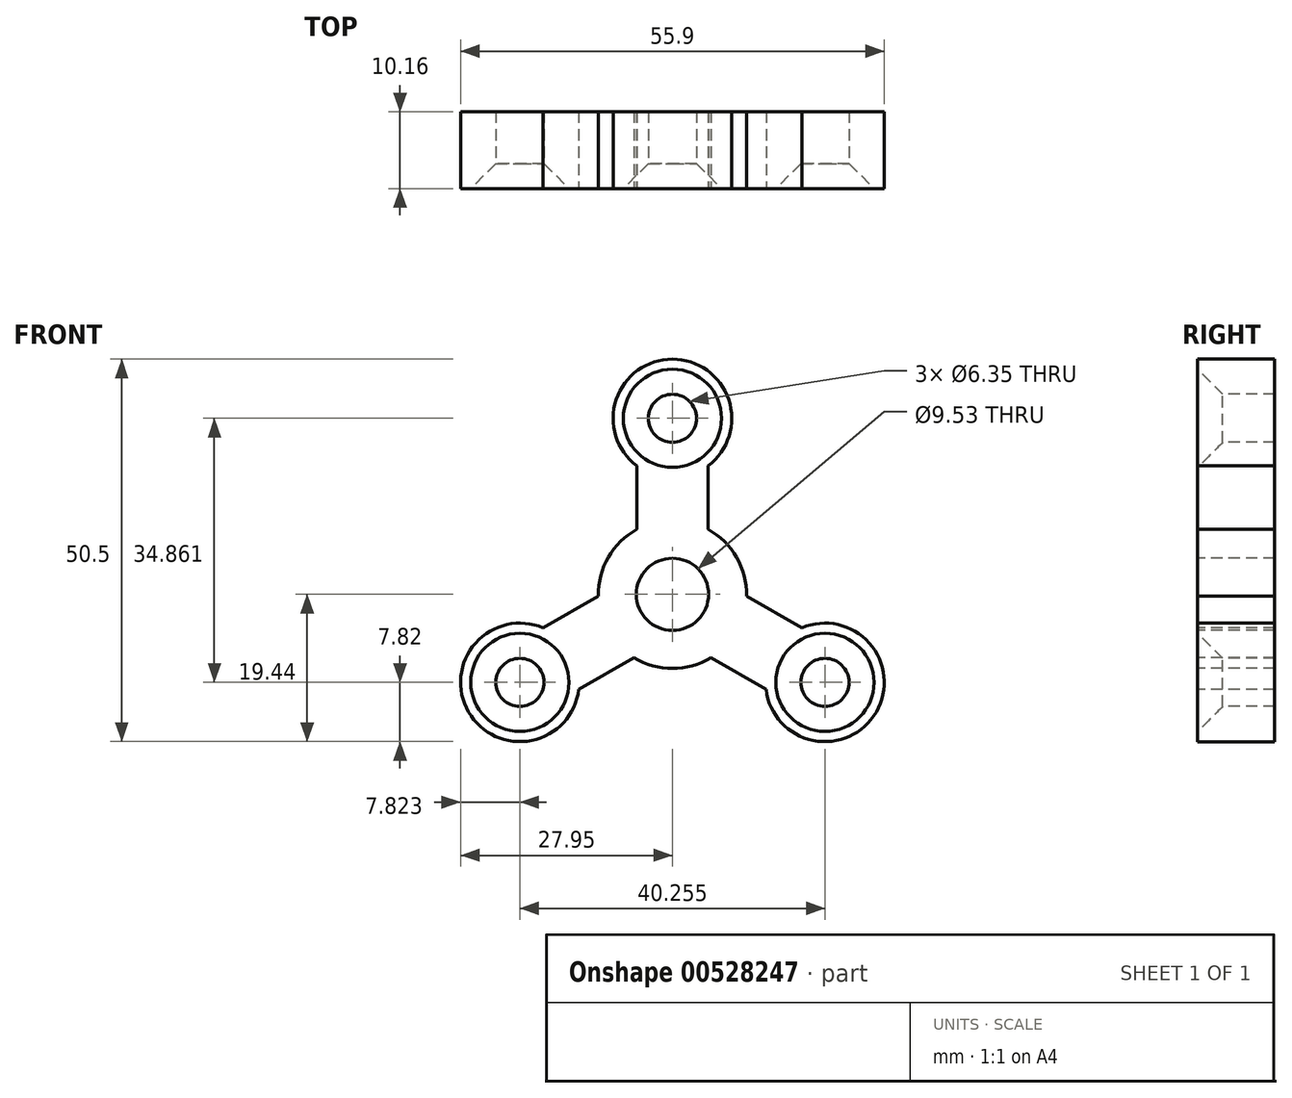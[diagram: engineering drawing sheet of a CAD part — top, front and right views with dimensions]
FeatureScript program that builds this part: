
annotation { "Feature Type Name" : "Feature", "Feature Type Description" : "" }
export const myFeature = defineFeature(function(context is Context, id is Id, definition is map)
    precondition{}
    {
        {
            var Q0;
            Q0=qCreatedBy(makeId("Front.planeOp"),FACE);
            var sketch = newSketch(context, id + "F0", { "sketchPlane" : qUnion([Q0])});
            skCircle(sketch, "E0", {"center": v(0, 0) * mm, "radius": 4.76 * mm});
            skCircle(sketch, "E1", {"center": v(0, 23.24) * mm, "radius": 3.18 * mm});
            skArc(sketch, "E2", {"start": v(4.7, 16.99) * mm, "mid": v(0, 31.06) * mm, "end": v(-4.7, 16.99) * mm});
            skArc(sketch, "E3", {"start": v(-4.7, 8.58) * mm, "mid": v(-8.47, 4.89) * mm, "end": v(-9.78, -0.22) * mm});
            skLineSegment(sketch, "E4", {"start": v(4.7, 8.58) * mm, "end": v(4.7, 16.99) * mm});
            skLineSegment(sketch, "E5", {"start": v(-4.7, 8.58) * mm, "end": v(-4.7, 16.99) * mm});
            skLineSegment(sketch, "E6.1.0", {"start": v(-5.08, -8.36) * mm, "end": v(-12.36, -12.56) * mm});
            skArc(sketch, "E6.1.1", {"start": v(-17.06, -4.42) * mm, "mid": v(-26.9, -15.53) * mm, "end": v(-12.36, -12.56) * mm});
            skLineSegment(sketch, "E6.1.2", {"start": v(-9.78, -0.22) * mm, "end": v(-17.06, -4.42) * mm});
            skLineSegment(sketch, "E6.2.0", {"start": v(9.78, -0.22) * mm, "end": v(17.06, -4.42) * mm});
            skArc(sketch, "E6.2.1", {"start": v(12.36, -12.56) * mm, "mid": v(26.9, -15.53) * mm, "end": v(17.06, -4.42) * mm});
            skLineSegment(sketch, "E6.2.2", {"start": v(5.08, -8.36) * mm, "end": v(12.36, -12.56) * mm});
            skArc(sketch, "E7.trimOffspring", {"start": v(-5.08, -8.36) * mm, "mid": v(0, -9.78) * mm, "end": v(5.08, -8.36) * mm});
            skArc(sketch, "E8.trimOffspring", {"start": v(9.78, -0.22) * mm, "mid": v(8.47, 4.89) * mm, "end": v(4.7, 8.58) * mm});
            skCircle(sketch, "E9", {"center": v(-20.13, -11.62) * mm, "radius": 3.18 * mm});
            skCircle(sketch, "E10", {"center": v(20.13, -11.62) * mm, "radius": 3.18 * mm});
            skSolve(sketch);
        }
        {
            var Q0;
            Q0=makeQuery(id+"F0.imprint","IMPRINT",FACE,{"disambiguationData":[TD([[makeQuery(id+"F0.imprint","IMPRINT",EDGE,{"derivedFrom":sQuery(id+"F0.wireOp",EDGE,"E0")}),-1.0]])]});
            extrude(context, id + "F1", {"entities" : qUnion([Q0]), "oppositeDirection" : true, "depth" : 10.16 * mm, "offsetDistance" : 25.4 * mm});
        }
        {
            var Q0;
            Q0=makeQuery(id+"F1.opExtrude","CAP_EDGE",EDGE,{"disambiguationData":[OSD([sQuery(id+"F0.wireOp",EDGE,"E1")])],"isStart":true});
            var Q1;
            Q1=makeQuery(id+"F1.opExtrude","CAP_EDGE",EDGE,{"disambiguationData":[OSD([sQuery(id+"F0.wireOp",EDGE,"E9")])],"isStart":true});
            var Q2;
            Q2=makeQuery(id+"F1.opExtrude","CAP_EDGE",EDGE,{"disambiguationData":[OSD([sQuery(id+"F0.wireOp",EDGE,"E10")])],"isStart":true});
            chamfer(context, id + "F2", {"entities" : qUnion([Q0, Q1, Q2]), "width" : 3.3 * mm, "tangentPropagation" : true});
        }
    });
